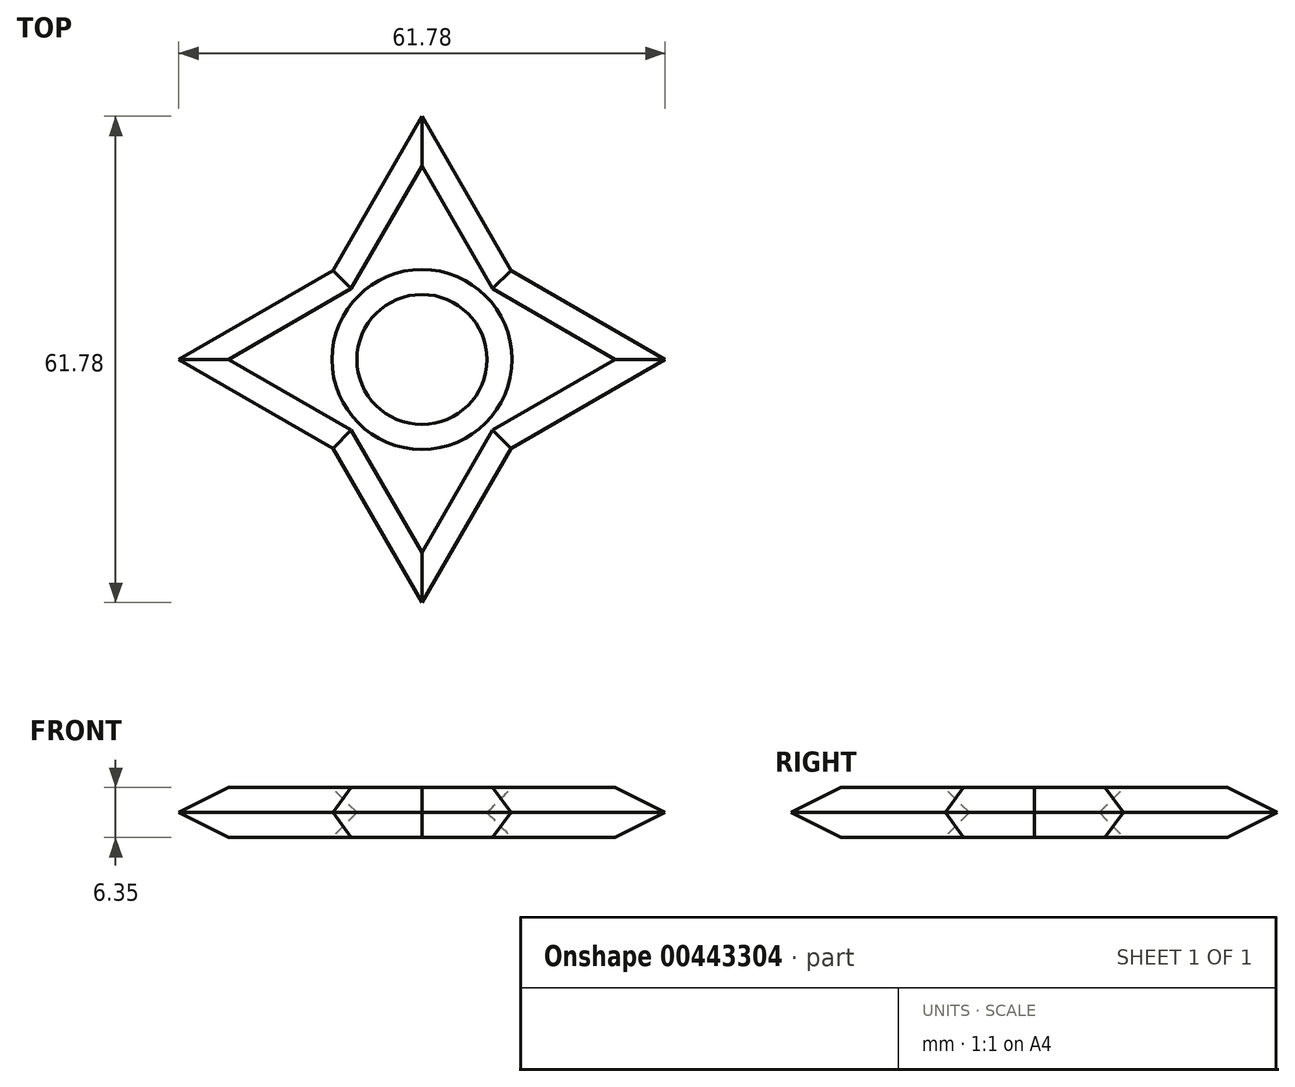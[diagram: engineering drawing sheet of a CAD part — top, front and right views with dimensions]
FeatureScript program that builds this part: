
annotation { "Feature Type Name" : "Feature", "Feature Type Description" : "" }
export const myFeature = defineFeature(function(context is Context, id is Id, definition is map)
    precondition{}
    {
        {
            var Q0;
            Q0=qCreatedBy(makeId("Top.planeOp"),FACE);
            var sketch = newSketch(context, id + "F0", { "sketchPlane" : qUnion([Q0])});
            skLineSegment(sketch, "E0.bottom", {"start": v(0, 0) * mm, "end": v(25.4, 0) * mm});
            skLineSegment(sketch, "E0.top", {"start": v(0, 25.4) * mm, "end": v(25.4, 25.4) * mm});
            skLineSegment(sketch, "E0.left", {"start": v(0, 0) * mm, "end": v(0, 25.4) * mm});
            skLineSegment(sketch, "E0.right", {"start": v(25.4, 0) * mm, "end": v(25.4, 25.4) * mm});
            skLineSegment(sketch, "E1", {"start": v(0, 25.4) * mm, "end": v(12.7, 47.4) * mm});
            skLineSegment(sketch, "E2", {"start": v(12.7, 47.4) * mm, "end": v(25.4, 25.4) * mm});
            skLineSegment(sketch, "E3", {"start": v(25.4, 0) * mm, "end": v(12.7, -22) * mm});
            skLineSegment(sketch, "E4", {"start": v(12.7, -22) * mm, "end": v(0, 0) * mm});
            skLineSegment(sketch, "E5", {"start": v(0, 0) * mm, "end": v(-22, 12.7) * mm});
            skLineSegment(sketch, "E6", {"start": v(-22, 12.7) * mm, "end": v(0, 25.4) * mm});
            skLineSegment(sketch, "E7", {"start": v(25.4, 25.4) * mm, "end": v(47.4, 12.7) * mm});
            skLineSegment(sketch, "E8", {"start": v(47.4, 12.7) * mm, "end": v(25.4, 0) * mm});
            skCircle(sketch, "E9", {"center": v(12.7, 12.7) * mm, "radius": 6.35 * mm});
            skPoint(sketch, "E9.centerSnap0", {"position": v(0, 12.7) * mm});
            skSolve(sketch);
        }
        {
            var Q0;
            Q0=makeQuery(id+"F0.imprint","IMPRINT",FACE,{"disambiguationData":[TD([[makeQuery(id+"F0.imprint","IMPRINT",EDGE,{"derivedFrom":sQuery(id+"F0.wireOp",EDGE,"E0.top")}),1.0]])]});
            var Q1;
            Q1=makeQuery(id+"F0.imprint","IMPRINT",FACE,{"disambiguationData":[TD([[makeQuery(id+"F0.imprint","IMPRINT",EDGE,{"derivedFrom":sQuery(id+"F0.wireOp",EDGE,"E0.bottom")}),1.0]])]});
            var Q2;
            Q2=makeQuery(id+"F0.imprint","IMPRINT",FACE,{"disambiguationData":[TD([[makeQuery(id+"F0.imprint","IMPRINT",EDGE,{"derivedFrom":sQuery(id+"F0.wireOp",EDGE,"E0.right")}),-1.0]])]});
            var Q3;
            Q3=makeQuery(id+"F0.imprint","IMPRINT",FACE,{"disambiguationData":[TD([[makeQuery(id+"F0.imprint","IMPRINT",EDGE,{"derivedFrom":sQuery(id+"F0.wireOp",EDGE,"E0.bottom")}),-1.0]])]});
            var Q4;
            Q4=makeQuery(id+"F0.imprint","IMPRINT",FACE,{"disambiguationData":[TD([[makeQuery(id+"F0.imprint","IMPRINT",EDGE,{"derivedFrom":sQuery(id+"F0.wireOp",EDGE,"E0.left")}),1.0]])]});
            extrude(context, id + "F1", {"entities" : qUnion([Q0, Q1, Q2, Q3, Q4]), "depth" : 6.35 * mm});
        }
        {
            var Q0;
            Q0=makeQuery(id+"F1.opExtrude","CAP_FACE",FACE,{"disambiguationData":[OSD([sQuery(id+"F0.wireOp",EDGE,"E1"),sQuery(id+"F0.wireOp",EDGE,"E2"),sQuery(id+"F0.wireOp",EDGE,"E3"),sQuery(id+"F0.wireOp",EDGE,"E4"),sQuery(id+"F0.wireOp",EDGE,"E5"),sQuery(id+"F0.wireOp",EDGE,"E6"),sQuery(id+"F0.wireOp",EDGE,"E7"),sQuery(id+"F0.wireOp",EDGE,"E8")])],"isStart":false});
            chamfer(context, id + "F2", {"entities" : qUnion([Q0]), "width" : 5.08 * mm, "tangentPropagation" : true});
        }
        {
            var Q0;
            Q0=makeQuery(id+"F1.opExtrude","CAP_EDGE",EDGE,{"disambiguationData":[OSD([sQuery(id+"F0.wireOp",EDGE,"E7")])],"isStart":true});
            var Q1;
            Q1=makeQuery(id+"F1.opExtrude","CAP_FACE",FACE,{"disambiguationData":[OSD([sQuery(id+"F0.wireOp",EDGE,"E1"),sQuery(id+"F0.wireOp",EDGE,"E2"),sQuery(id+"F0.wireOp",EDGE,"E3"),sQuery(id+"F0.wireOp",EDGE,"E4"),sQuery(id+"F0.wireOp",EDGE,"E5"),sQuery(id+"F0.wireOp",EDGE,"E6"),sQuery(id+"F0.wireOp",EDGE,"E7"),sQuery(id+"F0.wireOp",EDGE,"E8")])],"isStart":true});
            chamfer(context, id + "F3", {"entities" : qUnion([Q0, Q1]), "width" : 5.08 * mm, "tangentPropagation" : true});
        }
    });
